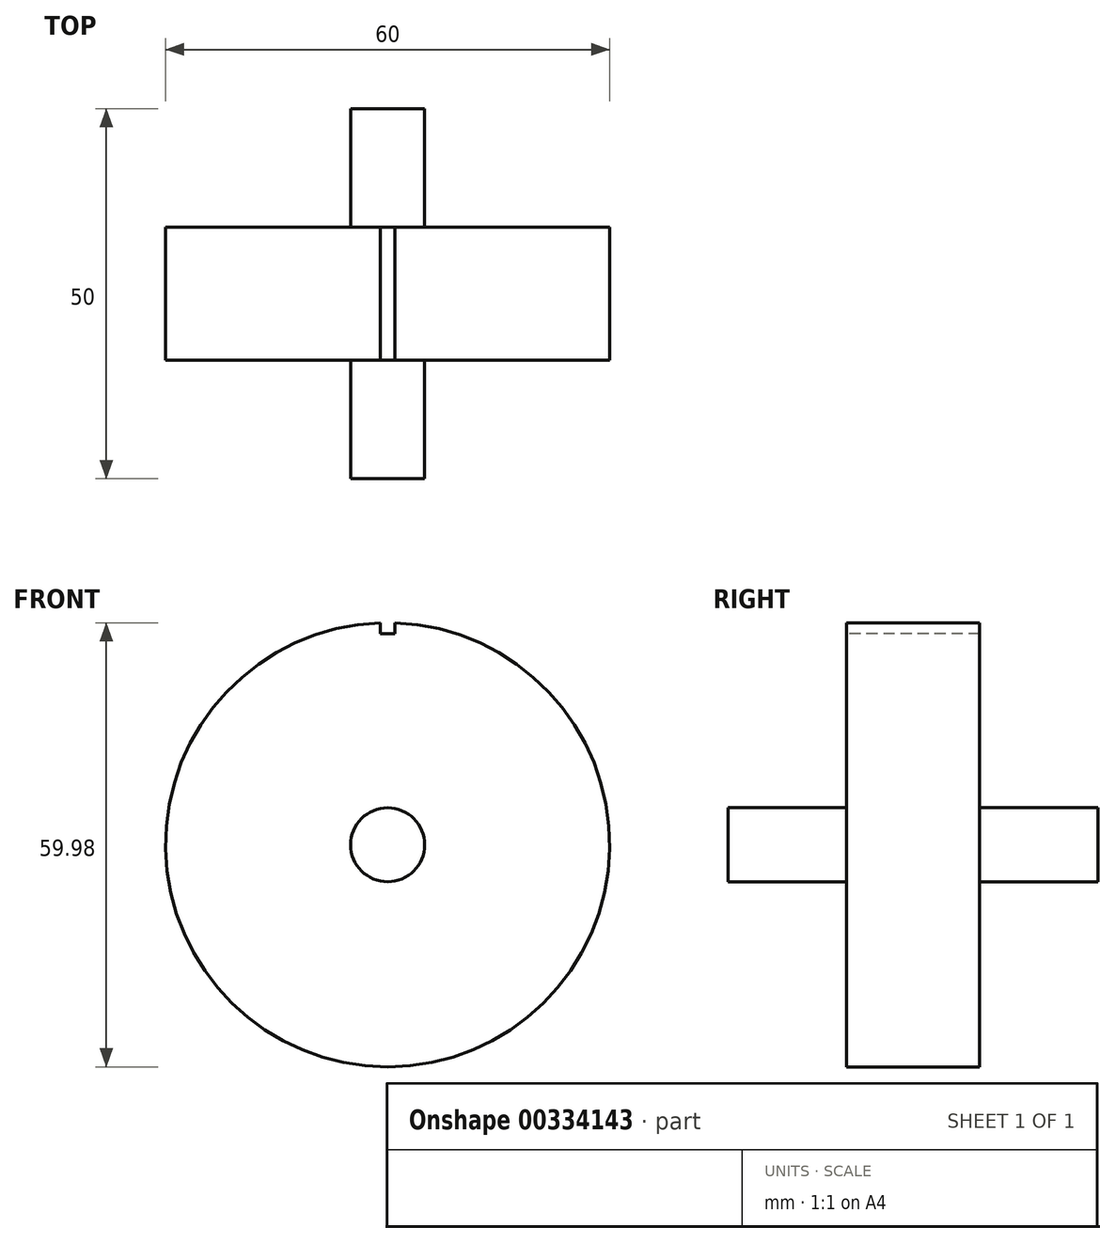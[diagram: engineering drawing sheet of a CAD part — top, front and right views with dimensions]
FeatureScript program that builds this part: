
annotation { "Feature Type Name" : "Feature", "Feature Type Description" : "" }
export const myFeature = defineFeature(function(context is Context, id is Id, definition is map)
    precondition{}
    {
        {
            var Q0;
            Q0=qCreatedBy(makeId("Front.planeOp"),FACE);
            var sketch = newSketch(context, id + "F0", { "sketchPlane" : qUnion([Q0])});
            skCircle(sketch, "E0", {"center": v(0, 0) * mm, "radius": 30 * mm});
            skCircle(sketch, "E1", {"center": v(0, 0) * mm, "radius": 5 * mm});
            skSolve(sketch);
        }
        {
            var Q0;
            Q0=makeQuery(id+"F0.imprint","IMPRINT",FACE,{"disambiguationData":[TD([[makeQuery(id+"F0.imprint","IMPRINT",EDGE,{"derivedFrom":sQuery(id+"F0.wireOp",EDGE,"E0")}),1.0]])]});
            extrude(context, id + "F1", {"entities" : qUnion([Q0]), "depth" : 18 * mm, "symmetric" : true});
        }
        {
            var Q0;
            Q0=makeQuery(id+"F0.imprint","IMPRINT",FACE,{"disambiguationData":[TD([[makeQuery(id+"F0.imprint","IMPRINT",EDGE,{"derivedFrom":sQuery(id+"F0.wireOp",EDGE,"E1")}),1.0]])]});
            extrude(context, id + "F2", {"entities" : qUnion([Q0]), "operationType" : NewBodyOperationType.ADD, "depth" : 50 * mm, "symmetric" : true});
        }
        {
            var Q0;
            Q0=makeQuery(id+"F1.opExtrude","CAP_FACE",FACE,{"disambiguationData":[OSD([sQuery(id+"F0.wireOp",EDGE,"E0"),sQuery(id+"F0.wireOp",EDGE,"E1")])],"isStart":false});
            var sketch = newSketch(context, id + "F3", { "sketchPlane" : qUnion([Q0])});
            skLineSegment(sketch, "E2.bottom", {"start": v(1, 31.5) * mm, "end": v(-1, 31.5) * mm});
            skLineSegment(sketch, "E2.top", {"start": v(1, 28.5) * mm, "end": v(-1, 28.5) * mm});
            skLineSegment(sketch, "E2.left", {"start": v(1, 31.5) * mm, "end": v(1, 28.5) * mm});
            skLineSegment(sketch, "E2.right", {"start": v(-1, 31.5) * mm, "end": v(-1, 28.5) * mm});
            skPoint(sketch, "E2.middle", {"position": v(0, 30) * mm});
            skSolve(sketch);
        }
        {
            var Q0;
            Q0 = qSketchRegion(id + "F3", true);
            extrude(context, id + "F4", {"entities" : qUnion([Q0]), "operationType" : NewBodyOperationType.REMOVE, "endBound" : BoundingType.THROUGH_ALL, "oppositeDirection" : true, "depth" : 25 * mm});
        }
        {
            var Q0;
            Q0=qCreatedBy(makeId("Top.planeOp"),FACE);
            var sketch = newSketch(context, id + "F5", { "sketchPlane" : qUnion([Q0])});
            skLineSegment(sketch, "E3", {"start": v(0, -70.77) * mm, "end": v(0, 58.15) * mm, "construction": true});
            skSolve(sketch);
        }
    });
